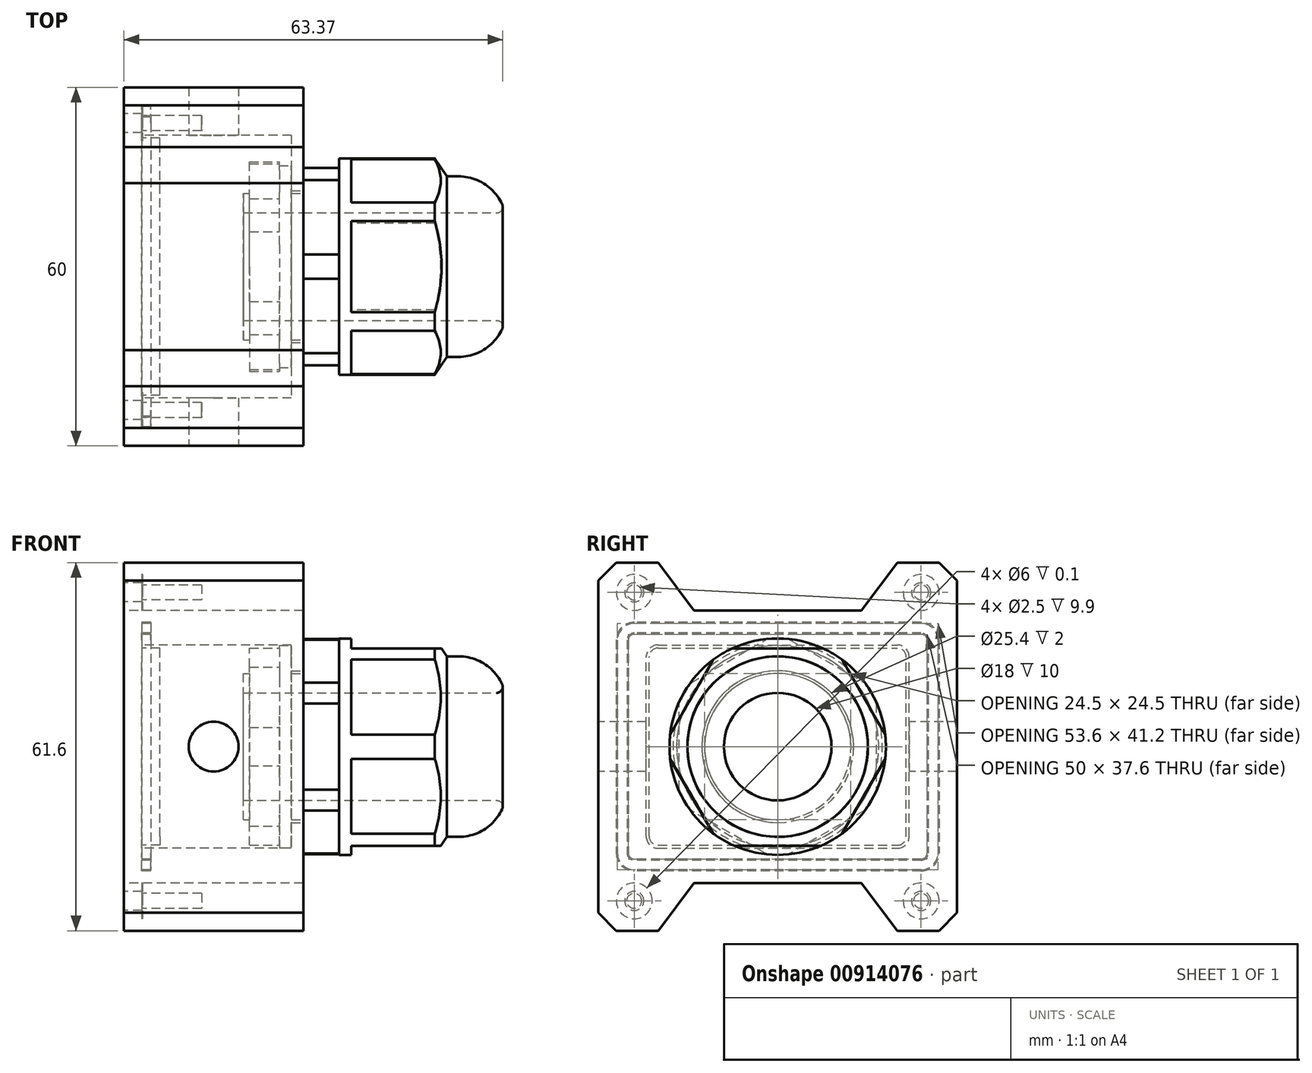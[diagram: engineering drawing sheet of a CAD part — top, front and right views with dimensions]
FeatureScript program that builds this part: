
annotation { "Feature Type Name" : "Feature", "Feature Type Description" : "" }
export const myFeature = defineFeature(function(context is Context, id is Id, definition is map)
    precondition{}
    {
        {
            var Q0;
            Q0=qCreatedBy(makeId("Top.planeOp"),FACE);
            var sketch = newSketch(context, id + "F0", { "sketchPlane" : qUnion([Q0])});
            skLineSegment(sketch, "E0.bottom", {"start": v(-15, 30) * mm, "end": v(15, 30) * mm});
            skLineSegment(sketch, "E0.top", {"start": v(-15, -30) * mm, "end": v(15, -30) * mm});
            skLineSegment(sketch, "E0.left", {"start": v(-15, 36) * mm, "end": v(-15, -30) * mm});
            skLineSegment(sketch, "E0.right", {"start": v(15, 36) * mm, "end": v(15, -30) * mm});
            skSolve(sketch);
        }
        {
            var Q0;
            Q0 = qSketchRegion(id + "F0", true);
            extrude(context, id + "F1", {"entities" : qUnion([Q0]), "endBound" : BoundingType.SYMMETRIC, "depth" : 45.6 * mm, "offsetDistance" : 25 * mm});
        }
        {
            var Q0;
            Q0=makeQuery(id+"F1.opExtrude","SWEPT_FACE",FACE,{"disambiguationData":[OSD([sQuery(id+"F0.wireOp",EDGE,"E0.left")])]});
            var sketch = newSketch(context, id + "F2", { "sketchPlane" : qUnion([Q0])});
            skLineSegment(sketch, "E1.bottom", {"start": v(-22, 17) * mm, "end": v(22, 17) * mm});
            skLineSegment(sketch, "E1.top", {"start": v(-22, -17) * mm, "end": v(22, -17) * mm});
            skLineSegment(sketch, "E1.left", {"start": v(-22, 17) * mm, "end": v(-22, -17) * mm});
            skLineSegment(sketch, "E1.right", {"start": v(22, 17) * mm, "end": v(22, -17) * mm});
            skSolve(sketch);
        }
        {
            var Q0;
            Q0 = qSketchRegion(id + "F2", true);
            extrude(context, id + "F3", {"entities" : qUnion([Q0]), "operationType" : NewBodyOperationType.REMOVE, "oppositeDirection" : true, "depth" : 28 * mm, "offsetDistance" : 25 * mm});
        }
        {
            var Q0;
            Q0=makeQuery(id+"F1.opExtrude","SWEPT_FACE",FACE,{"disambiguationData":[OSD([sQuery(id+"F0.wireOp",EDGE,"E0.top")])]});
            var sketch = newSketch(context, id + "F4", { "sketchPlane" : qUnion([Q0])});
            skCircle(sketch, "E2", {"center": v(0, 0) * mm, "radius": 4.17 * mm});
            skSolve(sketch);
        }
        {
            var Q0;
            Q0 = qSketchRegion(id + "F4", true);
            var Q1;
            Q1=makeQuery(id+"F1.opExtrude","SWEPT_FACE",FACE,{"disambiguationData":[OSD([sQuery(id+"F0.wireOp",EDGE,"E0.bottom")])]});
            extrude(context, id + "F5", {"entities" : qUnion([Q0]), "operationType" : NewBodyOperationType.REMOVE, "endBound" : BoundingType.UP_TO_SURFACE, "oppositeDirection" : true, "depth" : 25 * mm, "endBoundEntityFace" : qUnion([Q1]), "offsetDistance" : 25 * mm});
        }
        {
            var Q0;
            Q0=makeQuery(id+"F1.opExtrude","SWEPT_FACE",FACE,{"disambiguationData":[OSD([sQuery(id+"F0.wireOp",EDGE,"E0.right")])]});
            var sketch = newSketch(context, id + "F6", { "sketchPlane" : qUnion([Q0])});
            skCircle(sketch, "E3", {"center": v(0, 0) * mm, "radius": 12.7 * mm});
            skSolve(sketch);
        }
        {
            var Q0;
            Q0 = qSketchRegion(id + "F6", true);
            var Q1;
            Q1=makeQuery(id+"F3.boolean.opBoolean","COPY",FACE,{"derivedFrom":makeQuery(id+"F3.opExtrude","CAP_FACE",FACE,{"disambiguationData":[OSD([sQuery(id+"F2.wireOp",EDGE,"E1.bottom"),sQuery(id+"F2.wireOp",EDGE,"E1.top"),sQuery(id+"F2.wireOp",EDGE,"E1.left"),sQuery(id+"F2.wireOp",EDGE,"E1.right")])],"isStart":false})});
            extrude(context, id + "F7", {"entities" : qUnion([Q0]), "operationType" : NewBodyOperationType.REMOVE, "endBound" : BoundingType.UP_TO_SURFACE, "oppositeDirection" : true, "depth" : 25 * mm, "endBoundEntityFace" : qUnion([Q1]), "offsetDistance" : 25 * mm});
        }
        {
            var Q0;
            Q0=makeQuery(id+"F1.opExtrude","SWEPT_FACE",FACE,{"disambiguationData":[OSD([sQuery(id+"F0.wireOp",EDGE,"E0.top")])]});
            var sketch = newSketch(context, id + "F8", { "sketchPlane" : qUnion([Q0])});
            skLineSegment(sketch, "E4.bottom", {"start": v(-15, 22.8) * mm, "end": v(-12, 22.8) * mm});
            skLineSegment(sketch, "E4.top", {"start": v(-15, -22.8) * mm, "end": v(-12, -22.8) * mm});
            skLineSegment(sketch, "E4.left", {"start": v(-15, 22.8) * mm, "end": v(-15, -22.8) * mm});
            skLineSegment(sketch, "E4.right", {"start": v(-12, 22.8) * mm, "end": v(-12, -22.8) * mm});
            skSolve(sketch);
        }
        {
            var Q0;
            Q0 = qSketchRegion(id + "F8", true);
            var Q1;
            Q1=makeQuery(id+"F1.opExtrude","SWEPT_FACE",FACE,{"disambiguationData":[OSD([sQuery(id+"F0.wireOp",EDGE,"E0.bottom")])]});
            extrude(context, id + "F9", {"entities" : qUnion([Q0]), "operationType" : NewBodyOperationType.REMOVE, "endBound" : BoundingType.UP_TO_SURFACE, "oppositeDirection" : true, "depth" : 25 * mm, "endBoundEntityFace" : qUnion([Q1]), "offsetDistance" : 25 * mm});
        }
        {
            var Q0;
            Q0=makeQuery(id+"F9.boolean.opBoolean","COPY",FACE,{"derivedFrom":makeQuery(id+"F9.opExtrude","SWEPT_FACE",FACE,{"disambiguationData":[OSD([sQuery(id+"F8.wireOp",EDGE,"E4.right")])]})});
            var sketch = newSketch(context, id + "F10", { "sketchPlane" : qUnion([Q0])});
            skLineSegment(sketch, "E5.bottom", {"start": v(-25, 18.8) * mm, "end": v(25, 18.8) * mm});
            skLineSegment(sketch, "E5.top", {"start": v(-25, -18.8) * mm, "end": v(25, -18.8) * mm});
            skLineSegment(sketch, "E5.left", {"start": v(-25, 18.8) * mm, "end": v(-25, -18.8) * mm});
            skLineSegment(sketch, "E5.right", {"start": v(25, 18.8) * mm, "end": v(25, -18.8) * mm});
            skLineSegment(sketch, "E6.bottom", {"start": v(-27, 20.8) * mm, "end": v(27, 20.8) * mm});
            skLineSegment(sketch, "E6.top", {"start": v(-27, -20.8) * mm, "end": v(27, -20.8) * mm});
            skLineSegment(sketch, "E6.left", {"start": v(-27, 20.8) * mm, "end": v(-27, -20.8) * mm});
            skLineSegment(sketch, "E6.right", {"start": v(27, 20.8) * mm, "end": v(27, -20.8) * mm});
            skSolve(sketch);
        }
        {
            var Q0;
            Q0 = qSketchRegion(id + "F10", true);
            extrude(context, id + "F11", {"entities" : qUnion([Q0]), "operationType" : NewBodyOperationType.REMOVE, "oppositeDirection" : true, "depth" : 1.5 * mm, "offsetDistance" : 25 * mm});
        }
        {
            var Q0;
            Q0=makeQuery(id+"F11.boolean.opBoolean","COPY",EDGE,{"derivedFrom":makeQuery(id+"F11.opExtrude","SWEPT_EDGE",EDGE,{"disambiguationData":[OSD([sQuery(id+"F10.wireOp",EDGE,"E5.bottom"),sQuery(id+"F10.wireOp",EDGE,"E5.left")])]})});
            var Q1;
            Q1=makeQuery(id+"F11.boolean.opBoolean","COPY",EDGE,{"derivedFrom":makeQuery(id+"F11.opExtrude","SWEPT_EDGE",EDGE,{"disambiguationData":[OSD([sQuery(id+"F10.wireOp",EDGE,"E5.bottom"),sQuery(id+"F10.wireOp",EDGE,"E5.right")])]})});
            var Q2;
            Q2=makeQuery(id+"F11.boolean.opBoolean","COPY",EDGE,{"derivedFrom":makeQuery(id+"F11.opExtrude","SWEPT_EDGE",EDGE,{"disambiguationData":[OSD([sQuery(id+"F10.wireOp",EDGE,"E5.top"),sQuery(id+"F10.wireOp",EDGE,"E5.right")])]})});
            var Q3;
            Q3=makeQuery(id+"F11.boolean.opBoolean","COPY",EDGE,{"derivedFrom":makeQuery(id+"F11.opExtrude","SWEPT_EDGE",EDGE,{"disambiguationData":[OSD([sQuery(id+"F10.wireOp",EDGE,"E5.top"),sQuery(id+"F10.wireOp",EDGE,"E5.left")])]})});
            fillet(context, id + "F12", {"entities" : qUnion([Q0, Q1, Q2, Q3]), "radius" : 1 * mm, "tangentPropagation" : true, "allowEdgeOverflow" : false});
        }
        {
            var Q0;
            Q0=makeQuery(id+"F11.boolean.opBoolean","COPY",EDGE,{"derivedFrom":makeQuery(id+"F11.opExtrude","SWEPT_EDGE",EDGE,{"disambiguationData":[OSD([sQuery(id+"F10.wireOp",EDGE,"E6.bottom"),sQuery(id+"F10.wireOp",EDGE,"E6.left")])]})});
            var Q1;
            Q1=makeQuery(id+"F11.boolean.opBoolean","COPY",EDGE,{"derivedFrom":makeQuery(id+"F11.opExtrude","SWEPT_EDGE",EDGE,{"disambiguationData":[OSD([sQuery(id+"F10.wireOp",EDGE,"E6.bottom"),sQuery(id+"F10.wireOp",EDGE,"E6.right")])]})});
            var Q2;
            Q2=makeQuery(id+"F11.boolean.opBoolean","COPY",EDGE,{"derivedFrom":makeQuery(id+"F11.opExtrude","SWEPT_EDGE",EDGE,{"disambiguationData":[OSD([sQuery(id+"F10.wireOp",EDGE,"E6.top"),sQuery(id+"F10.wireOp",EDGE,"E6.right")])]})});
            var Q3;
            Q3=makeQuery(id+"F11.boolean.opBoolean","COPY",EDGE,{"derivedFrom":makeQuery(id+"F11.opExtrude","SWEPT_EDGE",EDGE,{"disambiguationData":[OSD([sQuery(id+"F10.wireOp",EDGE,"E6.top"),sQuery(id+"F10.wireOp",EDGE,"E6.left")])]})});
            fillet(context, id + "F13", {"entities" : qUnion([Q0, Q1, Q2, Q3]), "radius" : 3 * mm, "tangentPropagation" : true, "allowEdgeOverflow" : false});
        }
        {
            var Q0;
            Q0=makeQuery(id+"F3.boolean.opBoolean","COPY",EDGE,{"derivedFrom":makeQuery(id+"F3.opExtrude","SWEPT_EDGE",EDGE,{"disambiguationData":[OSD([sQuery(id+"F2.wireOp",EDGE,"E1.bottom"),sQuery(id+"F2.wireOp",EDGE,"E1.left")])]})});
            var Q1;
            Q1=makeQuery(id+"F3.boolean.opBoolean","COPY",EDGE,{"derivedFrom":makeQuery(id+"F3.opExtrude","SWEPT_EDGE",EDGE,{"disambiguationData":[OSD([sQuery(id+"F2.wireOp",EDGE,"E1.bottom"),sQuery(id+"F2.wireOp",EDGE,"E1.right")])]})});
            var Q2;
            Q2=makeQuery(id+"F3.boolean.opBoolean","COPY",EDGE,{"derivedFrom":makeQuery(id+"F3.opExtrude","SWEPT_EDGE",EDGE,{"disambiguationData":[OSD([sQuery(id+"F2.wireOp",EDGE,"E1.top"),sQuery(id+"F2.wireOp",EDGE,"E1.right")])]})});
            var Q3;
            Q3=makeQuery(id+"F3.boolean.opBoolean","COPY",EDGE,{"derivedFrom":makeQuery(id+"F3.opExtrude","SWEPT_EDGE",EDGE,{"disambiguationData":[OSD([sQuery(id+"F2.wireOp",EDGE,"E1.top"),sQuery(id+"F2.wireOp",EDGE,"E1.left")])]})});
            fillet(context, id + "F14", {"entities" : qUnion([Q0, Q1, Q2, Q3]), "radius" : 2 * mm, "tangentPropagation" : true, "allowEdgeOverflow" : false});
        }
        {
            var Q0;
            {var subQ3=sQuery(id+"F0.wireOp",EDGE,"E0.bottom");Q0=makeQuery(id+"F11.boolean.opBoolean","SPLIT",FACE,{"disambiguationData":[TD([makeQuery(id+"F1.opExtrude","SWEPT_FACE",FACE,{"disambiguationData":[OSD([subQ3])]})])],"derivedFrom":makeQuery(id+"F9.boolean.opBoolean","COPY",FACE,{"derivedFrom":makeQuery(id+"F9.opExtrude","SWEPT_FACE",FACE,{"disambiguationData":[OSD([sQuery(id+"F8.wireOp",EDGE,"E4.right")])]})})});}
            var sketch = newSketch(context, id + "F15", { "sketchPlane" : qUnion([Q0])});
            skLineSegment(sketch, "E7", {"start": v(-30, 22.8) * mm, "end": v(-30, 30.8) * mm});
            skLineSegment(sketch, "E8", {"start": v(-30, 30.8) * mm, "end": v(-20, 30.8) * mm});
            skLineSegment(sketch, "E9", {"start": v(-20, 30.8) * mm, "end": v(-14, 22.8) * mm});
            skLineSegment(sketch, "E10", {"start": v(-14, 22.8) * mm, "end": v(-30, 22.8) * mm});
            skLineSegment(sketch, "E11.MirrorCS", {"start": v(30, 30.8) * mm, "end": v(20, 30.8) * mm});
            skLineSegment(sketch, "E12.MirrorCS", {"start": v(14, 22.8) * mm, "end": v(30, 22.8) * mm});
            skLineSegment(sketch, "E13.MirrorCS", {"start": v(30, 22.8) * mm, "end": v(30, 30.8) * mm});
            skLineSegment(sketch, "E14.MirrorCS", {"start": v(20, 30.8) * mm, "end": v(14, 22.8) * mm});
            skLineSegment(sketch, "E15.MirrorCS", {"start": v(-30, -22.8) * mm, "end": v(-30, -30.8) * mm});
            skLineSegment(sketch, "E16.MirrorCS", {"start": v(30, -30.8) * mm, "end": v(20, -30.8) * mm});
            skLineSegment(sketch, "E17.MirrorCS", {"start": v(30, -22.8) * mm, "end": v(30, -30.8) * mm});
            skLineSegment(sketch, "E18.MirrorCS", {"start": v(-14, -22.8) * mm, "end": v(-30, -22.8) * mm});
            skLineSegment(sketch, "E19.MirrorCS", {"start": v(-20, -30.8) * mm, "end": v(-14, -22.8) * mm});
            skLineSegment(sketch, "E20.MirrorCS", {"start": v(-30, -30.8) * mm, "end": v(-20, -30.8) * mm});
            skLineSegment(sketch, "E21.MirrorCS", {"start": v(14, -22.8) * mm, "end": v(30, -22.8) * mm});
            skLineSegment(sketch, "E22.MirrorCS", {"start": v(20, -30.8) * mm, "end": v(14, -22.8) * mm});
            skSolve(sketch);
        }
        {
            var Q0;
            Q0 = qSketchRegion(id + "F15", true);
            var Q1;
            Q1=makeQuery(id+"F1.opExtrude","SWEPT_FACE",FACE,{"disambiguationData":[OSD([sQuery(id+"F0.wireOp",EDGE,"E0.right")])]});
            extrude(context, id + "F16", {"entities" : qUnion([Q0]), "operationType" : NewBodyOperationType.ADD, "endBound" : BoundingType.UP_TO_SURFACE, "oppositeDirection" : true, "depth" : 15 * mm, "endBoundEntityFace" : qUnion([Q1]), "offsetDistance" : 25 * mm});
        }
        {
            var Q0;
            {var subQ3=sQuery(id+"F0.wireOp",EDGE,"E0.bottom");Q0=makeQuery(id+"F16.boolean.opBoolean","MERGE",FACE,{"derivedFrom":[makeQuery(id+"F11.boolean.opBoolean","SPLIT",FACE,{"disambiguationData":[TD([makeQuery(id+"F1.opExtrude","SWEPT_FACE",FACE,{"disambiguationData":[OSD([subQ3])]})])],"derivedFrom":makeQuery(id+"F9.boolean.opBoolean","COPY",FACE,{"derivedFrom":makeQuery(id+"F9.opExtrude","SWEPT_FACE",FACE,{"disambiguationData":[OSD([sQuery(id+"F8.wireOp",EDGE,"E4.right")])]})})}),makeQuery(id+"F16.opExtrude","CAP_FACE",FACE,{"disambiguationData":[OSD([sQuery(id+"F15.wireOp",EDGE,"E7"),sQuery(id+"F15.wireOp",EDGE,"E8"),sQuery(id+"F15.wireOp",EDGE,"E9"),sQuery(id+"F15.wireOp",EDGE,"E10")])],"isStart":true}),makeQuery(id+"F16.opExtrude","CAP_FACE",FACE,{"disambiguationData":[OSD([sQuery(id+"F15.wireOp",EDGE,"E11.MirrorCS"),sQuery(id+"F15.wireOp",EDGE,"E12.MirrorCS"),sQuery(id+"F15.wireOp",EDGE,"E13.MirrorCS"),sQuery(id+"F15.wireOp",EDGE,"E14.MirrorCS")])],"isStart":true}),makeQuery(id+"F16.opExtrude","CAP_FACE",FACE,{"disambiguationData":[OSD([sQuery(id+"F15.wireOp",EDGE,"E15.MirrorCS"),sQuery(id+"F15.wireOp",EDGE,"E18.MirrorCS"),sQuery(id+"F15.wireOp",EDGE,"E19.MirrorCS"),sQuery(id+"F15.wireOp",EDGE,"E20.MirrorCS")])],"isStart":true}),makeQuery(id+"F16.opExtrude","CAP_FACE",FACE,{"disambiguationData":[OSD([sQuery(id+"F15.wireOp",EDGE,"E16.MirrorCS"),sQuery(id+"F15.wireOp",EDGE,"E17.MirrorCS"),sQuery(id+"F15.wireOp",EDGE,"E21.MirrorCS"),sQuery(id+"F15.wireOp",EDGE,"E22.MirrorCS")])],"isStart":true})]});}
            var sketch = newSketch(context, id + "F17", { "sketchPlane" : qUnion([Q0])});
            skCircle(sketch, "E23", {"center": v(-24, 25.8) * mm, "radius": 1.25 * mm});
            skCircle(sketch, "E24.MirrorC", {"center": v(24, 25.8) * mm, "radius": 1.25 * mm});
            skCircle(sketch, "E25.MirrorC", {"center": v(24, -25.8) * mm, "radius": 1.25 * mm});
            skCircle(sketch, "E26.MirrorC", {"center": v(-24, -25.8) * mm, "radius": 1.25 * mm});
            skSolve(sketch);
        }
        {
            var Q0;
            Q0 = qSketchRegion(id + "F17", true);
            extrude(context, id + "F18", {"entities" : qUnion([Q0]), "operationType" : NewBodyOperationType.REMOVE, "oppositeDirection" : true, "depth" : 10 * mm, "offsetDistance" : 25 * mm});
        }
        {
            var Q0;
            {var subQ3=sQuery(id+"F0.wireOp",EDGE,"E0.bottom");Q0=makeQuery(id+"F16.boolean.opBoolean","MERGE",FACE,{"derivedFrom":[makeQuery(id+"F11.boolean.opBoolean","SPLIT",FACE,{"disambiguationData":[TD([makeQuery(id+"F1.opExtrude","SWEPT_FACE",FACE,{"disambiguationData":[OSD([subQ3])]})])],"derivedFrom":makeQuery(id+"F9.boolean.opBoolean","COPY",FACE,{"derivedFrom":makeQuery(id+"F9.opExtrude","SWEPT_FACE",FACE,{"disambiguationData":[OSD([sQuery(id+"F8.wireOp",EDGE,"E4.right")])]})})}),makeQuery(id+"F16.opExtrude","CAP_FACE",FACE,{"disambiguationData":[OSD([sQuery(id+"F15.wireOp",EDGE,"E7"),sQuery(id+"F15.wireOp",EDGE,"E8"),sQuery(id+"F15.wireOp",EDGE,"E9"),sQuery(id+"F15.wireOp",EDGE,"E10")])],"isStart":true}),makeQuery(id+"F16.opExtrude","CAP_FACE",FACE,{"disambiguationData":[OSD([sQuery(id+"F15.wireOp",EDGE,"E11.MirrorCS"),sQuery(id+"F15.wireOp",EDGE,"E12.MirrorCS"),sQuery(id+"F15.wireOp",EDGE,"E13.MirrorCS"),sQuery(id+"F15.wireOp",EDGE,"E14.MirrorCS")])],"isStart":true}),makeQuery(id+"F16.opExtrude","CAP_FACE",FACE,{"disambiguationData":[OSD([sQuery(id+"F15.wireOp",EDGE,"E15.MirrorCS"),sQuery(id+"F15.wireOp",EDGE,"E18.MirrorCS"),sQuery(id+"F15.wireOp",EDGE,"E19.MirrorCS"),sQuery(id+"F15.wireOp",EDGE,"E20.MirrorCS")])],"isStart":true}),makeQuery(id+"F16.opExtrude","CAP_FACE",FACE,{"disambiguationData":[OSD([sQuery(id+"F15.wireOp",EDGE,"E16.MirrorCS"),sQuery(id+"F15.wireOp",EDGE,"E17.MirrorCS"),sQuery(id+"F15.wireOp",EDGE,"E21.MirrorCS"),sQuery(id+"F15.wireOp",EDGE,"E22.MirrorCS")])],"isStart":true})]});}
            var sketch = newSketch(context, id + "F19", { "sketchPlane" : qUnion([Q0])});
            skCircle(sketch, "E27", {"center": v(-24, 25.8) * mm, "radius": 3 * mm});
            skCircle(sketch, "E28.MirrorC", {"center": v(24, 25.8) * mm, "radius": 3 * mm});
            skCircle(sketch, "E29.MirrorC", {"center": v(24, -25.8) * mm, "radius": 3 * mm});
            skCircle(sketch, "E30.MirrorC", {"center": v(-24, -25.8) * mm, "radius": 3 * mm});
            skSolve(sketch);
        }
        {
            var Q0;
            Q0 = qSketchRegion(id + "F19", true);
            extrude(context, id + "F20", {"entities" : qUnion([Q0]), "operationType" : NewBodyOperationType.REMOVE, "oppositeDirection" : true, "depth" : 0.1 * mm, "offsetDistance" : 25 * mm});
        }
        {
            var Q0;
            Q0=makeQuery(id+"F16.opExtrude","SWEPT_EDGE",EDGE,{"disambiguationData":[OSD([sQuery(id+"F15.wireOp",EDGE,"E11.MirrorCS"),sQuery(id+"F15.wireOp",EDGE,"E13.MirrorCS")])]});
            var Q1;
            Q1=makeQuery(id+"F16.opExtrude","SWEPT_EDGE",EDGE,{"disambiguationData":[OSD([sQuery(id+"F15.wireOp",EDGE,"E7"),sQuery(id+"F15.wireOp",EDGE,"E8")])]});
            var Q2;
            Q2=makeQuery(id+"F16.opExtrude","SWEPT_EDGE",EDGE,{"disambiguationData":[OSD([sQuery(id+"F15.wireOp",EDGE,"E16.MirrorCS"),sQuery(id+"F15.wireOp",EDGE,"E17.MirrorCS")])]});
            var Q3;
            Q3=makeQuery(id+"F16.opExtrude","SWEPT_EDGE",EDGE,{"disambiguationData":[OSD([sQuery(id+"F15.wireOp",EDGE,"E15.MirrorCS"),sQuery(id+"F15.wireOp",EDGE,"E20.MirrorCS")])]});
            chamfer(context, id + "F21", {"entities" : qUnion([Q0, Q1, Q2, Q3]), "width" : 3 * mm, "tangentPropagation" : true});
        }
        {
            var Q0;
            {var subQ3=sQuery(id+"F0.wireOp",EDGE,"E0.bottom");Q0=makeQuery(id+"F11.boolean.opBoolean","SPLIT",FACE,{"disambiguationData":[TD([makeQuery(id+"F1.opExtrude","SWEPT_FACE",FACE,{"disambiguationData":[OSD([subQ3])]})])],"derivedFrom":makeQuery(id+"F9.boolean.opBoolean","COPY",FACE,{"derivedFrom":makeQuery(id+"F9.opExtrude","SWEPT_FACE",FACE,{"disambiguationData":[OSD([sQuery(id+"F8.wireOp",EDGE,"E4.right")])]})})});}
            var sketch = newSketch(context, id + "F22", { "sketchPlane" : qUnion([Q0])});
            skLineSegment(sketch, "E31.0.0", {"start": v(30, 22.8) * mm, "end": v(-30, 22.8) * mm});
            skLineSegment(sketch, "E31.0.2", {"start": v(-30, 22.8) * mm, "end": v(-30, -22.8) * mm});
            skLineSegment(sketch, "E31.0.4", {"start": v(-30, -22.8) * mm, "end": v(30, -22.8) * mm});
            skLineSegment(sketch, "E31.0.6", {"start": v(30, -22.8) * mm, "end": v(30, 22.8) * mm});
            skSolve(sketch);
        }
        {
            var Q0;
            Q0 = qSketchRegion(id + "F22", true);
            extrude(context, id + "F23", {"entities" : qUnion([Q0]), "depth" : 3 * mm, "offsetDistance" : 25 * mm});
        }
        {
            var Q0;
            Q0=makeQuery(id+"F23.opExtrude","CAP_FACE",FACE,{"disambiguationData":[OSD([sQuery(id+"F22.wireOp",EDGE,"E31.0.0"),sQuery(id+"F22.wireOp",EDGE,"E31.0.2"),sQuery(id+"F22.wireOp",EDGE,"E31.0.4"),sQuery(id+"F22.wireOp",EDGE,"E31.0.6")])],"isStart":true});
            var sketch = newSketch(context, id + "F24", { "sketchPlane" : qUnion([Q0])});
            skLineSegment(sketch, "E32.0", {"start": v(30, 30.8) * mm, "end": v(20, 30.8) * mm});
            skLineSegment(sketch, "E33.0", {"start": v(20, 30.8) * mm, "end": v(14, 22.8) * mm});
            skLineSegment(sketch, "E34", {"start": v(30, 30.8) * mm, "end": v(30, 22.8) * mm});
            skLineSegment(sketch, "E35", {"start": v(14, 22.8) * mm, "end": v(30, 22.8) * mm});
            skLineSegment(sketch, "E36.MirrorCS", {"start": v(-14, 22.8) * mm, "end": v(-30, 22.8) * mm});
            skLineSegment(sketch, "E37.MirrorCS", {"start": v(-20, 30.8) * mm, "end": v(-14, 22.8) * mm});
            skLineSegment(sketch, "E38.MirrorCS", {"start": v(-30, 30.8) * mm, "end": v(-30, 22.8) * mm});
            skLineSegment(sketch, "E39.MirrorCS", {"start": v(-20, 30.8) * mm, "end": v(-30, 30.8) * mm});
            skLineSegment(sketch, "E40.MirrorCS", {"start": v(14, -22.8) * mm, "end": v(30, -22.8) * mm});
            skLineSegment(sketch, "E41.MirrorCS", {"start": v(20, -30.8) * mm, "end": v(14, -22.8) * mm});
            skLineSegment(sketch, "E42.MirrorCS", {"start": v(30, -30.8) * mm, "end": v(30, -22.8) * mm});
            skLineSegment(sketch, "E43.MirrorCS", {"start": v(-14, -22.8) * mm, "end": v(-30, -22.8) * mm});
            skLineSegment(sketch, "E44.MirrorCS", {"start": v(20, -30.8) * mm, "end": v(30, -30.8) * mm});
            skLineSegment(sketch, "E45.MirrorCS", {"start": v(-20, -30.8) * mm, "end": v(-30, -30.8) * mm});
            skLineSegment(sketch, "E46.MirrorCS", {"start": v(-30, -30.8) * mm, "end": v(-30, -22.8) * mm});
            skLineSegment(sketch, "E47.MirrorCS", {"start": v(-20, -30.8) * mm, "end": v(-14, -22.8) * mm});
            skSolve(sketch);
        }
        {
            var Q0;
            Q0 = qSketchRegion(id + "F24", true);
            var Q1;
            Q1=makeQuery(id+"F23.opExtrude","CAP_FACE",FACE,{"disambiguationData":[OSD([sQuery(id+"F22.wireOp",EDGE,"E31.0.0"),sQuery(id+"F22.wireOp",EDGE,"E31.0.2"),sQuery(id+"F22.wireOp",EDGE,"E31.0.4"),sQuery(id+"F22.wireOp",EDGE,"E31.0.6")])],"isStart":false});
            extrude(context, id + "F25", {"entities" : qUnion([Q0]), "operationType" : NewBodyOperationType.ADD, "endBound" : BoundingType.UP_TO_SURFACE, "oppositeDirection" : true, "depth" : 25 * mm, "endBoundEntityFace" : qUnion([Q1]), "offsetDistance" : 25 * mm});
        }
        {
            var Q0;
            Q0=makeQuery(id+"F25.boolean.opBoolean","MERGE",FACE,{"derivedFrom":[makeQuery(id+"F23.opExtrude","CAP_FACE",FACE,{"disambiguationData":[OSD([sQuery(id+"F22.wireOp",EDGE,"E31.0.0"),sQuery(id+"F22.wireOp",EDGE,"E31.0.2"),sQuery(id+"F22.wireOp",EDGE,"E31.0.4"),sQuery(id+"F22.wireOp",EDGE,"E31.0.6")])],"isStart":false}),makeQuery(id+"F25.opExtrude","CAP_FACE",FACE,{"disambiguationData":[OSD([sQuery(id+"F24.wireOp",EDGE,"E32.0"),sQuery(id+"F24.wireOp",EDGE,"E34"),sQuery(id+"F24.wireOp",EDGE,"E35"),sQuery(id+"F24.wireOp",EDGE,"E33.0")])],"isStart":false}),makeQuery(id+"F25.opExtrude","CAP_FACE",FACE,{"disambiguationData":[OSD([sQuery(id+"F24.wireOp",EDGE,"E36.MirrorCS"),sQuery(id+"F24.wireOp",EDGE,"E37.MirrorCS"),sQuery(id+"F24.wireOp",EDGE,"E38.MirrorCS"),sQuery(id+"F24.wireOp",EDGE,"E39.MirrorCS")])],"isStart":false}),makeQuery(id+"F25.opExtrude","CAP_FACE",FACE,{"disambiguationData":[OSD([sQuery(id+"F24.wireOp",EDGE,"E41.MirrorCS"),sQuery(id+"F24.wireOp",EDGE,"E40.MirrorCS"),sQuery(id+"F24.wireOp",EDGE,"E44.MirrorCS"),sQuery(id+"F24.wireOp",EDGE,"E42.MirrorCS")])],"isStart":false}),makeQuery(id+"F25.opExtrude","CAP_FACE",FACE,{"disambiguationData":[OSD([sQuery(id+"F24.wireOp",EDGE,"E43.MirrorCS"),sQuery(id+"F24.wireOp",EDGE,"E45.MirrorCS"),sQuery(id+"F24.wireOp",EDGE,"E46.MirrorCS"),sQuery(id+"F24.wireOp",EDGE,"E47.MirrorCS")])],"isStart":false})]});
            var sketch = newSketch(context, id + "F26", { "sketchPlane" : qUnion([Q0])});
            skCircle(sketch, "E48", {"center": v(-24, 25.8) * mm, "radius": 1.6 * mm});
            skCircle(sketch, "E49.MirrorC", {"center": v(24, 25.8) * mm, "radius": 1.6 * mm});
            skCircle(sketch, "E50.MirrorC", {"center": v(24, -25.8) * mm, "radius": 1.6 * mm});
            skCircle(sketch, "E51.MirrorC", {"center": v(-24, -25.8) * mm, "radius": 1.6 * mm});
            skSolve(sketch);
        }
        {
            var Q0;
            Q0 = qSketchRegion(id + "F26", true);
            var Q1;
            Q1=makeQuery(id+"F25.boolean.opBoolean","MERGE",FACE,{"derivedFrom":[makeQuery(id+"F23.opExtrude","CAP_FACE",FACE,{"disambiguationData":[OSD([sQuery(id+"F22.wireOp",EDGE,"E31.0.0"),sQuery(id+"F22.wireOp",EDGE,"E31.0.2"),sQuery(id+"F22.wireOp",EDGE,"E31.0.4"),sQuery(id+"F22.wireOp",EDGE,"E31.0.6")])],"isStart":true}),makeQuery(id+"F25.opExtrude","CAP_FACE",FACE,{"disambiguationData":[OSD([sQuery(id+"F24.wireOp",EDGE,"E32.0"),sQuery(id+"F24.wireOp",EDGE,"E34"),sQuery(id+"F24.wireOp",EDGE,"E35"),sQuery(id+"F24.wireOp",EDGE,"E33.0")])],"isStart":true}),makeQuery(id+"F25.opExtrude","CAP_FACE",FACE,{"disambiguationData":[OSD([sQuery(id+"F24.wireOp",EDGE,"E36.MirrorCS"),sQuery(id+"F24.wireOp",EDGE,"E37.MirrorCS"),sQuery(id+"F24.wireOp",EDGE,"E38.MirrorCS"),sQuery(id+"F24.wireOp",EDGE,"E39.MirrorCS")])],"isStart":true}),makeQuery(id+"F25.opExtrude","CAP_FACE",FACE,{"disambiguationData":[OSD([sQuery(id+"F24.wireOp",EDGE,"E41.MirrorCS"),sQuery(id+"F24.wireOp",EDGE,"E40.MirrorCS"),sQuery(id+"F24.wireOp",EDGE,"E44.MirrorCS"),sQuery(id+"F24.wireOp",EDGE,"E42.MirrorCS")])],"isStart":true}),makeQuery(id+"F25.opExtrude","CAP_FACE",FACE,{"disambiguationData":[OSD([sQuery(id+"F24.wireOp",EDGE,"E43.MirrorCS"),sQuery(id+"F24.wireOp",EDGE,"E45.MirrorCS"),sQuery(id+"F24.wireOp",EDGE,"E46.MirrorCS"),sQuery(id+"F24.wireOp",EDGE,"E47.MirrorCS")])],"isStart":true})]});
            extrude(context, id + "F27", {"entities" : qUnion([Q0]), "operationType" : NewBodyOperationType.REMOVE, "endBound" : BoundingType.UP_TO_SURFACE, "oppositeDirection" : true, "depth" : 25 * mm, "endBoundEntityFace" : qUnion([Q1]), "offsetDistance" : 25 * mm});
        }
        {
            var Q0;
            Q0=makeQuery(id+"F23.opExtrude","CAP_FACE",FACE,{"disambiguationData":[OSD([sQuery(id+"F22.wireOp",EDGE,"E31.0.0"),sQuery(id+"F22.wireOp",EDGE,"E31.0.1"),sQuery(id+"F22.wireOp",EDGE,"E31.0.2"),sQuery(id+"F22.wireOp",EDGE,"E31.0.3"),sQuery(id+"F22.wireOp",EDGE,"E31.0.4"),sQuery(id+"F22.wireOp",EDGE,"E31.0.5"),sQuery(id+"F22.wireOp",EDGE,"E31.0.6"),sQuery(id+"F22.wireOp",EDGE,"E31.0.7")])],"isStart":true});
            var sketch = newSketch(context, id + "F28", { "sketchPlane" : qUnion([Q0])});
            skLineSegment(sketch, "E52.0", {"start": v(-20, 16.5) * mm, "end": v(20, 16.5) * mm});
            skLineSegment(sketch, "E52.1", {"start": v(-21.5, -15) * mm, "end": v(-21.5, 15) * mm});
            skLineSegment(sketch, "E52.2", {"start": v(-20, -16.5) * mm, "end": v(20, -16.5) * mm});
            skLineSegment(sketch, "E52.3", {"start": v(21.5, -15) * mm, "end": v(21.5, 15) * mm});
            skArc(sketch, "E53.0", {"start": v(-20, 16.5) * mm, "mid": v(-21.06, 16.06) * mm, "end": v(-21.5, 15) * mm});
            skArc(sketch, "E54.0", {"start": v(-21.5, -15) * mm, "mid": v(-21.06, -16.06) * mm, "end": v(-20, -16.5) * mm});
            skArc(sketch, "E55.0", {"start": v(20, -16.5) * mm, "mid": v(21.06, -16.06) * mm, "end": v(21.5, -15) * mm});
            skArc(sketch, "E56.0", {"start": v(21.5, 15) * mm, "mid": v(21.06, 16.06) * mm, "end": v(20, 16.5) * mm});
            skSolve(sketch);
        }
        {
            var Q0;
            Q0 = qSketchRegion(id + "F28", true);
            extrude(context, id + "F29", {"entities" : qUnion([Q0]), "operationType" : NewBodyOperationType.ADD, "depth" : 3 * mm, "offsetDistance" : 25 * mm});
        }
        {
            var Q0;
            Q0=makeQuery(id+"F23.opExtrude","CAP_FACE",FACE,{"disambiguationData":[OSD([sQuery(id+"F22.wireOp",EDGE,"E31.0.0"),sQuery(id+"F22.wireOp",EDGE,"E31.0.1"),sQuery(id+"F22.wireOp",EDGE,"E31.0.2"),sQuery(id+"F22.wireOp",EDGE,"E31.0.3"),sQuery(id+"F22.wireOp",EDGE,"E31.0.4"),sQuery(id+"F22.wireOp",EDGE,"E31.0.5"),sQuery(id+"F22.wireOp",EDGE,"E31.0.6"),sQuery(id+"F22.wireOp",EDGE,"E31.0.7")])],"isStart":true});
            var sketch = newSketch(context, id + "F30", { "sketchPlane" : qUnion([Q0])});
            skLineSegment(sketch, "E57.0", {"start": v(24, 20.6) * mm, "end": v(-24, 20.6) * mm});
            skLineSegment(sketch, "E57.1", {"start": v(26.8, 17.8) * mm, "end": v(26.8, -17.8) * mm});
            skLineSegment(sketch, "E57.2", {"start": v(24, -20.6) * mm, "end": v(-24, -20.6) * mm});
            skLineSegment(sketch, "E57.3", {"start": v(-26.8, 17.8) * mm, "end": v(-26.8, -17.8) * mm});
            skArc(sketch, "E58.0", {"start": v(-24, 20.6) * mm, "mid": v(-25.98, 19.78) * mm, "end": v(-26.8, 17.8) * mm});
            skArc(sketch, "E59.0", {"start": v(-26.8, -17.8) * mm, "mid": v(-25.98, -19.78) * mm, "end": v(-24, -20.6) * mm});
            skArc(sketch, "E60.0", {"start": v(24, -20.6) * mm, "mid": v(25.98, -19.78) * mm, "end": v(26.8, -17.8) * mm});
            skArc(sketch, "E61.0", {"start": v(26.8, 17.8) * mm, "mid": v(25.98, 19.78) * mm, "end": v(24, 20.6) * mm});
            skArc(sketch, "E62.0", {"start": v(24, 19) * mm, "mid": v(24.85, 18.65) * mm, "end": v(25.2, 17.8) * mm});
            skLineSegment(sketch, "E62.1", {"start": v(25.2, 17.8) * mm, "end": v(25.2, -17.8) * mm});
            skLineSegment(sketch, "E62.2", {"start": v(24, 19) * mm, "end": v(-24, 19) * mm});
            skArc(sketch, "E62.3", {"start": v(25.2, -17.8) * mm, "mid": v(24.85, -18.65) * mm, "end": v(24, -19) * mm});
            skArc(sketch, "E62.4", {"start": v(-25.2, 17.8) * mm, "mid": v(-24.85, 18.65) * mm, "end": v(-24, 19) * mm});
            skLineSegment(sketch, "E62.5", {"start": v(-25.2, 17.8) * mm, "end": v(-25.2, -17.8) * mm});
            skArc(sketch, "E62.6", {"start": v(-24, -19) * mm, "mid": v(-24.85, -18.65) * mm, "end": v(-25.2, -17.8) * mm});
            skLineSegment(sketch, "E62.7", {"start": v(24, -19) * mm, "end": v(-24, -19) * mm});
            skSolve(sketch);
        }
        {
            var Q0;
            Q0 = qSketchRegion(id + "F30", true);
            extrude(context, id + "F31", {"entities" : qUnion([Q0]), "operationType" : NewBodyOperationType.ADD, "depth" : 1.5 * mm, "offsetDistance" : 25 * mm});
        }
        {
            var Q0;
            Q0=makeQuery(id+"F25.opExtrude","SWEPT_EDGE",EDGE,{"disambiguationData":[OSD([sQuery(id+"F24.wireOp",EDGE,"E38.MirrorCS"),sQuery(id+"F24.wireOp",EDGE,"E39.MirrorCS")])]});
            var Q1;
            Q1=makeQuery(id+"F25.opExtrude","SWEPT_EDGE",EDGE,{"disambiguationData":[OSD([sQuery(id+"F24.wireOp",EDGE,"E32.0"),sQuery(id+"F24.wireOp",EDGE,"E34")])]});
            var Q2;
            Q2=makeQuery(id+"F25.opExtrude","SWEPT_EDGE",EDGE,{"disambiguationData":[OSD([sQuery(id+"F24.wireOp",EDGE,"E45.MirrorCS"),sQuery(id+"F24.wireOp",EDGE,"E46.MirrorCS")])]});
            var Q3;
            Q3=makeQuery(id+"F25.opExtrude","SWEPT_EDGE",EDGE,{"disambiguationData":[OSD([sQuery(id+"F24.wireOp",EDGE,"E44.MirrorCS"),sQuery(id+"F24.wireOp",EDGE,"E42.MirrorCS")])]});
            chamfer(context, id + "F32", {"entities" : qUnion([Q0, Q1, Q2, Q3]), "width" : 3 * mm, "tangentPropagation" : true});
        }
        {
            var Q0;
            Q0=makeQuery(id+"F1.opExtrude","SWEPT_FACE",FACE,{"disambiguationData":[OSD([sQuery(id+"F0.wireOp",EDGE,"E0.right")])]});
            var sketch = newSketch(context, id + "F33", { "sketchPlane" : qUnion([Q0])});
            skCircle(sketch, "E63", {"center": v(0, 0) * mm, "radius": 12.25 * mm});
            skSolve(sketch);
        }
        {
            var Q0;
            Q0 = qSketchRegion(id + "F33", true);
            extrude(context, id + "F34", {"entities" : qUnion([Q0]), "oppositeDirection" : true, "depth" : 10 * mm, "offsetDistance" : 25 * mm});
        }
        {
            var Q0;
            Q0=makeQuery(id+"F3.boolean.opBoolean","COPY",FACE,{"derivedFrom":makeQuery(id+"F3.opExtrude","CAP_FACE",FACE,{"disambiguationData":[OSD([sQuery(id+"F2.wireOp",EDGE,"E1.bottom"),sQuery(id+"F2.wireOp",EDGE,"E1.top"),sQuery(id+"F2.wireOp",EDGE,"E1.left"),sQuery(id+"F2.wireOp",EDGE,"E1.right")])],"isStart":false})});
            var sketch = newSketch(context, id + "F35", { "sketchPlane" : qUnion([Q0])});
            skCircle(sketch, "E64", {"center": v(0, 0) * mm, "radius": 12.25 * mm});
            skCircle(sketch, "E65", {"center": v(0, 0) * mm, "radius": 16.9 * mm});
            skSolve(sketch);
        }
        {
            var Q0;
            Q0 = qSketchRegion(id + "F35", true);
            extrude(context, id + "F36", {"entities" : qUnion([Q0]), "operationType" : NewBodyOperationType.ADD, "depth" : 2 * mm, "offsetDistance" : 25 * mm});
        }
        {
            var Q0;
            Q0=makeQuery(id+"F36.opExtrude","CAP_FACE",FACE,{"disambiguationData":[OSD([sQuery(id+"F35.wireOp",EDGE,"E64"),sQuery(id+"F35.wireOp",EDGE,"E65")])],"isStart":false});
            var sketch = newSketch(context, id + "F37", { "sketchPlane" : qUnion([Q0])});
            skArc(sketch, "E66", {"start": v(5.83, -16.5) * mm, "mid": v(8.75, -15.16) * mm, "end": v(11.37, -13.3) * mm});
            skLineSegment(sketch, "E67", {"start": v(11.37, -13.3) * mm, "end": v(17.2, -3.2) * mm});
            skLineSegment(sketch, "E68", {"start": v(17.2, 3.2) * mm, "end": v(11.37, 13.3) * mm});
            skLineSegment(sketch, "E69", {"start": v(5.83, 16.5) * mm, "end": v(-5.83, 16.5) * mm});
            skLineSegment(sketch, "E70", {"start": v(-11.37, 13.3) * mm, "end": v(-17.2, 3.2) * mm});
            skLineSegment(sketch, "E71", {"start": v(-17.2, -3.2) * mm, "end": v(-11.37, -13.3) * mm});
            skLineSegment(sketch, "E72", {"start": v(-5.83, -16.5) * mm, "end": v(5.83, -16.5) * mm});
            skPoint(sketch, "E73.orphan", {"position": v(9.53, -16.5) * mm});
            skArc(sketch, "E74.trimOffspring", {"start": v(17.2, -3.2) * mm, "mid": v(17.5, 0) * mm, "end": v(17.2, 3.2) * mm});
            skPoint(sketch, "E75.orphan", {"position": v(19.05, 0) * mm});
            skArc(sketch, "E76.trimOffspring", {"start": v(11.37, 13.3) * mm, "mid": v(8.75, 15.16) * mm, "end": v(5.83, 16.5) * mm});
            skArc(sketch, "E77.trimOffspring", {"start": v(-5.83, 16.5) * mm, "mid": v(-8.75, 15.16) * mm, "end": v(-11.37, 13.3) * mm});
            skArc(sketch, "E78.trimOffspring", {"start": v(-17.2, 3.2) * mm, "mid": v(-17.5, 0) * mm, "end": v(-17.2, -3.2) * mm});
            skPoint(sketch, "E79.orphan", {"position": v(-19.05, 0) * mm});
            skArc(sketch, "E80.trimOffspring", {"start": v(-11.37, -13.3) * mm, "mid": v(-8.75, -15.16) * mm, "end": v(-5.83, -16.5) * mm});
            skPoint(sketch, "E81.orphan", {"position": v(-9.53, -16.5) * mm});
            skSolve(sketch);
        }
        {
            var Q0;
            Q0 = qSketchRegion(id + "F37", true);
            extrude(context, id + "F38", {"entities" : qUnion([Q0]), "operationType" : NewBodyOperationType.ADD, "depth" : 5 * mm, "offsetDistance" : 25 * mm});
        }
        {
            var Q0;
            Q0=makeQuery(id+"F34.opExtrude","CAP_FACE",FACE,{"disambiguationData":[OSD([sQuery(id+"F33.wireOp",EDGE,"E63")])],"isStart":true});
            var sketch = newSketch(context, id + "F39", { "sketchPlane" : qUnion([Q0])});
            skCircle(sketch, "E82", {"center": v(0, 0) * mm, "radius": 9 * mm});
            skSolve(sketch);
        }
        {
            var Q0;
            Q0 = qSketchRegion(id + "F39", true);
            var Q1;
            Q1=makeQuery(id+"F34.opExtrude","CAP_FACE",FACE,{"disambiguationData":[OSD([sQuery(id+"F33.wireOp",EDGE,"E63")])],"isStart":false});
            extrude(context, id + "F40", {"entities" : qUnion([Q0]), "operationType" : NewBodyOperationType.REMOVE, "endBound" : BoundingType.UP_TO_SURFACE, "oppositeDirection" : true, "depth" : 25 * mm, "endBoundEntityFace" : qUnion([Q1]), "offsetDistance" : 25 * mm});
        }
        {
            var Q0;
            Q0=makeQuery(id+"F34.opExtrude","CAP_FACE",FACE,{"disambiguationData":[OSD([sQuery(id+"F33.wireOp",EDGE,"E63")])],"isStart":true});
            var sketch = newSketch(context, id + "F41", { "sketchPlane" : qUnion([Q0])});
            skArc(sketch, "E83", {"start": v(-14.48, 10.7) * mm, "mid": v(-15.59, 9) * mm, "end": v(-16.5, 7.2) * mm});
            skLineSegment(sketch, "E84", {"start": v(-2.02, 17.89) * mm, "end": v(-14.48, 10.7) * mm});
            skLineSegment(sketch, "E85", {"start": v(-16.5, 7.2) * mm, "end": v(-16.5, -7.2) * mm});
            skLineSegment(sketch, "E86", {"start": v(-14.48, -10.7) * mm, "end": v(-2.02, -17.89) * mm});
            skLineSegment(sketch, "E87", {"start": v(2.02, -17.89) * mm, "end": v(14.48, -10.7) * mm});
            skLineSegment(sketch, "E88", {"start": v(16.5, -7.2) * mm, "end": v(16.5, 7.2) * mm});
            skLineSegment(sketch, "E89", {"start": v(14.48, 10.7) * mm, "end": v(2.02, 17.89) * mm});
            skPoint(sketch, "E90.orphan", {"position": v(0, 19.05) * mm});
            skArc(sketch, "E91.trimOffspring", {"start": v(2.02, 17.89) * mm, "mid": v(0, 18) * mm, "end": v(-2.02, 17.89) * mm});
            skPoint(sketch, "E92.orphan", {"position": v(16.5, 9.53) * mm});
            skArc(sketch, "E93.trimOffspring", {"start": v(16.5, 7.2) * mm, "mid": v(15.59, 9) * mm, "end": v(14.48, 10.7) * mm});
            skPoint(sketch, "E94.orphan", {"position": v(16.5, -9.53) * mm});
            skArc(sketch, "E95.trimOffspring", {"start": v(14.48, -10.7) * mm, "mid": v(15.59, -9) * mm, "end": v(16.5, -7.2) * mm});
            skPoint(sketch, "E96.orphan", {"position": v(0, -19.05) * mm});
            skArc(sketch, "E97.trimOffspring", {"start": v(-2.02, -17.89) * mm, "mid": v(0, -18) * mm, "end": v(2.02, -17.89) * mm});
            skArc(sketch, "E98.trimOffspring", {"start": v(-16.5, -7.2) * mm, "mid": v(-15.59, -9) * mm, "end": v(-14.48, -10.7) * mm});
            skSolve(sketch);
        }
        {
            var Q0;
            Q0 = qSketchRegion(id + "F41", true);
            extrude(context, id + "F42", {"entities" : qUnion([Q0]), "depth" : 8 * mm, "offsetDistance" : 25 * mm});
        }
        {
            var Q0;
            Q0=makeQuery(id+"F42.opExtrude","CAP_FACE",FACE,{"disambiguationData":[OSD([sQuery(id+"F41.wireOp",EDGE,"E83"),sQuery(id+"F41.wireOp",EDGE,"E84"),sQuery(id+"F41.wireOp",EDGE,"E85"),sQuery(id+"F41.wireOp",EDGE,"E86"),sQuery(id+"F41.wireOp",EDGE,"E87"),sQuery(id+"F41.wireOp",EDGE,"E88"),sQuery(id+"F41.wireOp",EDGE,"E89"),sQuery(id+"F41.wireOp",EDGE,"E91.trimOffspring"),sQuery(id+"F41.wireOp",EDGE,"E93.trimOffspring"),sQuery(id+"F41.wireOp",EDGE,"E95.trimOffspring"),sQuery(id+"F41.wireOp",EDGE,"E97.trimOffspring"),sQuery(id+"F41.wireOp",EDGE,"E98.trimOffspring")])],"isStart":false});
            var sketch = newSketch(context, id + "F43", { "sketchPlane" : qUnion([Q0])});
            skArc(sketch, "E99", {"start": v(-7.64, 16.4) * mm, "mid": v(-9.24, 15.56) * mm, "end": v(-10.75, 14.56) * mm});
            skLineSegment(sketch, "E100", {"start": v(-7.64, 16.4) * mm, "end": v(7.64, 16.4) * mm});
            skLineSegment(sketch, "E101", {"start": v(10.75, 14.56) * mm, "end": v(17.99, 2.03) * mm});
            skLineSegment(sketch, "E102", {"start": v(17.99, -2.03) * mm, "end": v(10.75, -14.56) * mm});
            skLineSegment(sketch, "E103", {"start": v(7.23, -16.6) * mm, "end": v(-7.23, -16.6) * mm});
            skLineSegment(sketch, "E104", {"start": v(-10.75, -14.56) * mm, "end": v(-17.99, -2.03) * mm});
            skLineSegment(sketch, "E105", {"start": v(-17.99, 2.03) * mm, "end": v(-10.75, 14.56) * mm});
            skArc(sketch, "E106.trimOffspring", {"start": v(-17.99, 2.03) * mm, "mid": v(-18.1, 0) * mm, "end": v(-17.99, -2.03) * mm});
            skArc(sketch, "E107.trimOffspring", {"start": v(-10.75, -14.56) * mm, "mid": v(-9.05, -15.68) * mm, "end": v(-7.23, -16.6) * mm});
            skArc(sketch, "E108.trimOffspring", {"start": v(7.23, -16.6) * mm, "mid": v(9.05, -15.68) * mm, "end": v(10.75, -14.56) * mm});
            skArc(sketch, "E109.trimOffspring", {"start": v(17.99, -2.03) * mm, "mid": v(18.1, 0) * mm, "end": v(17.99, 2.03) * mm});
            skArc(sketch, "E110.trimOffspring", {"start": v(10.75, 14.56) * mm, "mid": v(9.24, 15.56) * mm, "end": v(7.64, 16.4) * mm});
            skPoint(sketch, "E111.orphan", {"position": v(-9.69, 16.4) * mm});
            skPoint(sketch, "E112.orphan", {"position": v(-19.16, 0) * mm});
            skPoint(sketch, "E113.orphan", {"position": v(19.16, 0) * mm});
            skPoint(sketch, "E114.orphan", {"position": v(9.69, 16.4) * mm});
            skSolve(sketch);
        }
        {
            var Q0;
            Q0 = qSketchRegion(id + "F43", true);
            extrude(context, id + "F44", {"entities" : qUnion([Q0]), "operationType" : NewBodyOperationType.ADD, "depth" : 16 * mm, "offsetDistance" : 25 * mm});
        }
        {
            var Q0;
            {var subQ0=sQuery(id+"F43.wireOp",EDGE,"E105");var subQ1=sQuery(id+"F43.wireOp",EDGE,"E104");var subQ2=sQuery(id+"F41.wireOp",EDGE,"E85");var subQ3=sQuery(id+"F43.wireOp",EDGE,"E106.trimOffspring");Q0=makeQuery(id+"F44.boolean.opBoolean","SPLIT",FACE,{"disambiguationData":[TD([makeQuery(id+"F42.opExtrude","SWEPT_FACE",FACE,{"disambiguationData":[OSD([subQ2])]})])],"derivedFrom":makeQuery(id+"F44.opExtrude","CAP_FACE",FACE,{"disambiguationData":[OSD([sQuery(id+"F43.wireOp",EDGE,"E99"),sQuery(id+"F43.wireOp",EDGE,"E100"),sQuery(id+"F43.wireOp",EDGE,"E101"),sQuery(id+"F43.wireOp",EDGE,"E102"),sQuery(id+"F43.wireOp",EDGE,"E103"),subQ1,subQ0,subQ3,sQuery(id+"F43.wireOp",EDGE,"E107.trimOffspring"),sQuery(id+"F43.wireOp",EDGE,"E108.trimOffspring"),sQuery(id+"F43.wireOp",EDGE,"E109.trimOffspring"),sQuery(id+"F43.wireOp",EDGE,"E110.trimOffspring")])],"isStart":true})});}
            var sketch = newSketch(context, id + "F45", { "sketchPlane" : qUnion([Q0])});
            skCircle(sketch, "E115", {"center": v(0, 0) * mm, "radius": 18.1 * mm});
            skSolve(sketch);
        }
        {
            var Q0;
            Q0 = qSketchRegion(id + "F45", true);
            extrude(context, id + "F46", {"entities" : qUnion([Q0]), "operationType" : NewBodyOperationType.ADD, "depth" : 2 * mm, "offsetDistance" : 25 * mm});
        }
        {
            var Q0;
            Q0=qCreatedBy(makeId("Top.planeOp"),FACE);
            var sketch = newSketch(context, id + "F47", { "sketchPlane" : qUnion([Q0])});
            skLineSegment(sketch, "E116", {"start": v(39, 18.1) * mm, "end": v(39, 15.1) * mm});
            skLineSegment(sketch, "E117", {"start": v(39, 15.1) * mm, "end": v(37, 18.1) * mm});
            skLineSegment(sketch, "E118", {"start": v(37, 18.1) * mm, "end": v(39, 18.1) * mm});
            skSolve(sketch);
        }
        {
            var Q0;
            Q0=makeQuery(id+"F44.opExtrude","CAP_FACE",FACE,{"disambiguationData":[OSD([sQuery(id+"F43.wireOp",EDGE,"E99"),sQuery(id+"F43.wireOp",EDGE,"E100"),sQuery(id+"F43.wireOp",EDGE,"E101"),sQuery(id+"F43.wireOp",EDGE,"E102"),sQuery(id+"F43.wireOp",EDGE,"E103"),sQuery(id+"F43.wireOp",EDGE,"E104"),sQuery(id+"F43.wireOp",EDGE,"E105"),sQuery(id+"F43.wireOp",EDGE,"E106.trimOffspring"),sQuery(id+"F43.wireOp",EDGE,"E107.trimOffspring"),sQuery(id+"F43.wireOp",EDGE,"E108.trimOffspring"),sQuery(id+"F43.wireOp",EDGE,"E109.trimOffspring"),sQuery(id+"F43.wireOp",EDGE,"E110.trimOffspring")])],"isStart":false});
            var sketch = newSketch(context, id + "F48", { "sketchPlane" : qUnion([Q0])});
            skCircle(sketch, "E119", {"center": v(0, 0) * mm, "radius": 18.1 * mm});
            skSolve(sketch);
        }
        {
            var Q0;
            Q0 = qSketchRegion(id + "F47", true);
            var Q1;
            Q1=sQuery(id+"F48.wireOp",EDGE,"E119");
            sweep(context, id + "F49", {"operationType" : NewBodyOperationType.REMOVE, "profiles" : qUnion([Q0]), "path" : qUnion([Q1])});
        }
        {
            var Q0;
            Q0=makeQuery(id+"F44.opExtrude","CAP_FACE",FACE,{"disambiguationData":[OSD([sQuery(id+"F43.wireOp",EDGE,"E99"),sQuery(id+"F43.wireOp",EDGE,"E100"),sQuery(id+"F43.wireOp",EDGE,"E101"),sQuery(id+"F43.wireOp",EDGE,"E102"),sQuery(id+"F43.wireOp",EDGE,"E103"),sQuery(id+"F43.wireOp",EDGE,"E104"),sQuery(id+"F43.wireOp",EDGE,"E105"),sQuery(id+"F43.wireOp",EDGE,"E106.trimOffspring"),sQuery(id+"F43.wireOp",EDGE,"E107.trimOffspring"),sQuery(id+"F43.wireOp",EDGE,"E108.trimOffspring"),sQuery(id+"F43.wireOp",EDGE,"E109.trimOffspring"),sQuery(id+"F43.wireOp",EDGE,"E110.trimOffspring")])],"isStart":false});
            var sketch = newSketch(context, id + "F50", { "sketchPlane" : qUnion([Q0])});
            skCircle(sketch, "E120", {"center": v(0, 0) * mm, "radius": 15.1 * mm});
            skSolve(sketch);
        }
        {
            var Q0;
            Q0 = qSketchRegion(id + "F50", true);
            extrude(context, id + "F51", {"entities" : qUnion([Q0]), "operationType" : NewBodyOperationType.ADD, "depth" : 10 * mm, "offsetDistance" : 25 * mm});
        }
        {
            var Q0;
            Q0=makeQuery(id+"F51.opExtrude","CAP_EDGE",EDGE,{"disambiguationData":[OSD([sQuery(id+"F50.wireOp",EDGE,"E120")])],"isStart":false});
            fillet(context, id + "F52", {"entities" : qUnion([Q0]), "radius" : 8 * mm, "tangentPropagation" : true, "allowEdgeOverflow" : false});
        }
        {
            var Q0;
            Q0=makeQuery(id+"F51.opExtrude","CAP_FACE",FACE,{"disambiguationData":[OSD([sQuery(id+"F50.wireOp",EDGE,"E120")])],"isStart":false});
            var sketch = newSketch(context, id + "F53", { "sketchPlane" : qUnion([Q0])});
            skCircle(sketch, "E121", {"center": v(0, 0) * mm, "radius": 9 * mm});
            skSolve(sketch);
        }
        {
            var Q0;
            Q0 = qSketchRegion(id + "F53", true);
            var Q1;
            Q1=makeQuery(id+"F34.opExtrude","CAP_FACE",FACE,{"disambiguationData":[OSD([sQuery(id+"F33.wireOp",EDGE,"E63")])],"isStart":false});
            extrude(context, id + "F54", {"entities" : qUnion([Q0]), "operationType" : NewBodyOperationType.REMOVE, "endBound" : BoundingType.UP_TO_SURFACE, "oppositeDirection" : true, "depth" : 25 * mm, "endBoundEntityFace" : qUnion([Q1]), "offsetDistance" : 25 * mm});
        }
        {
            var Q0;
            Q0=makeQuery(id+"F54.boolean.opBoolean","INTERSECT",EDGE,{"derivedFrom":[makeQuery(id+"F52.opFillet","BLEND_FACE",FACE,{"disambiguationData":[OSD([sQuery(id+"F50.wireOp",EDGE,"E120")])]}),makeQuery(id+"F54.opExtrude","SWEPT_FACE",FACE,{"disambiguationData":[OSD([sQuery(id+"F53.wireOp",EDGE,"E121")])]})]});
            fillet(context, id + "F55", {"entities" : qUnion([Q0]), "radius" : 1 * mm, "tangentPropagation" : true, "allowEdgeOverflow" : false});
        }
    });
